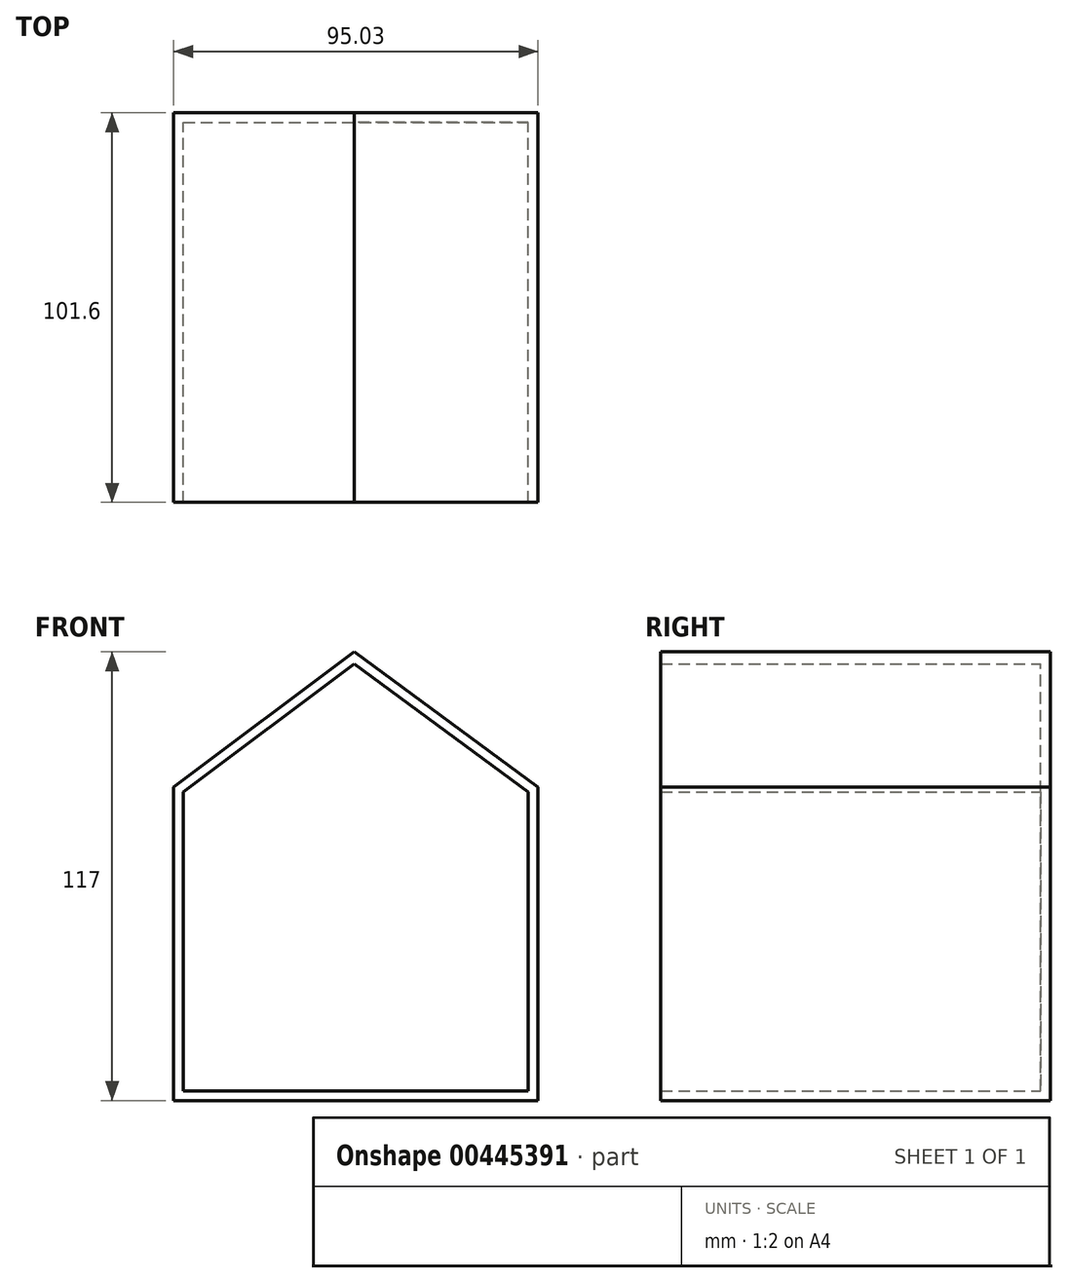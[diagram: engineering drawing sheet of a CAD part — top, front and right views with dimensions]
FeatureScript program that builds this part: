
annotation { "Feature Type Name" : "Feature", "Feature Type Description" : "" }
export const myFeature = defineFeature(function(context is Context, id is Id, definition is map)
    precondition{}
    {
        {
            var Q0;
            Q0=qCreatedBy(makeId("Front.planeOp"),FACE);
            var sketch = newSketch(context, id + "F0", { "sketchPlane" : qUnion([Q0])});
            skLineSegment(sketch, "E0", {"start": v(-47.05, 18.1) * mm, "end": v(-47.05, -63.6) * mm});
            skLineSegment(sketch, "E1", {"start": v(-47.05, -63.6) * mm, "end": v(47.98, -63.6) * mm});
            skLineSegment(sketch, "E2", {"start": v(47.98, -63.6) * mm, "end": v(47.98, 18.1) * mm});
            skLineSegment(sketch, "E3", {"start": v(-47.05, 18.1) * mm, "end": v(47.98, 18.1) * mm});
            skLineSegment(sketch, "E4", {"start": v(-47.05, 18.1) * mm, "end": v(0, 53.4) * mm});
            skLineSegment(sketch, "E5", {"start": v(47.98, 18.1) * mm, "end": v(0, 53.4) * mm});
            skSolve(sketch);
        }
        {
            var Q0;
            Q0 = qSketchRegion(id + "F0", true);
            extrude(context, id + "F1", {"entities" : qUnion([Q0]), "depth" : 101.6 * mm});
        }
        {
            var Q0;
            Q0=makeQuery(id+"F1.opExtrude","CAP_FACE",FACE,{"disambiguationData":[OSD([sQuery(id+"F0.wireOp",EDGE,"E0"),sQuery(id+"F0.wireOp",EDGE,"E1"),sQuery(id+"F0.wireOp",EDGE,"E2"),sQuery(id+"F0.wireOp",EDGE,"E4"),sQuery(id+"F0.wireOp",EDGE,"E5")])],"isStart":false});
            shell(context, id + "F2", {"entities" : qUnion([Q0]), "thickness" : 2.54 * mm});
        }
    });
